# Revit family: stepp
name_source: partatom
category: Furniture
revit_build: Autodesk Revit 2015 (Build: 20140903_1530(x64)
units: mm (PartAtom-declared; Revit-internal decimal feet)

## types (4) — shared parameters
BIMobject category = Furniture
Date of publishing = 2016-03-22
Design country = Sweden
Edition number = 1
IFC Classification = Furnishing Element
Manufacturer country = Sweden
Manufacturer name = Swedese
Material main = Steel
Material secondary = Fabric
Nominal height = 1010
Nominal width = 780
OmniClass Code = 23-21 11 00
OmniClass Description = Commercial Furniture
Product Guid = 392f2ee7-836a-4807-9f35-b5779e80a406
Product SKU = 14701
Product data url = https://bimobject.com
Product family = Easy chairs
Product group = Stepp
Product name = Stepp
QR code = http://bimobject.com
Steel = No
Technical description = https://static-swedese.s3.amazonaws.com
UNSPSC Code = 56
Uniclass 1.4 Code = L8211
Uniclass 1.4 Description = Furniture
Weight Net (Kg) = 25
Wood = Yes
zero-valued in all types: BOSUseNativeGeometries

## type names (no varying parameters)
- COLOUR - (Black) TYPE - (Steel)
- COLOUR - (Red) TYPE - (Steel)
- COLOUR - (Black) TYPE - (Wood)
- COLOUR - (Red) TYPE - (Wood)

## geometry (parser evidence)
native form markers: Sweep x2
no freeform markers — native parametric forms only
